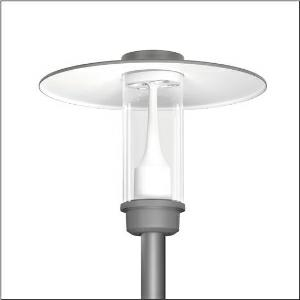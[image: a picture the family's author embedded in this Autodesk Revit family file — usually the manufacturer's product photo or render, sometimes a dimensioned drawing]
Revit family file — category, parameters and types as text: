
# Revit family: litepole_2_iq___p1_0a_5xa5425nf14hp_e36f
name_source: partatom
category: Lighting Fixtures
units: mm (PartAtom-declared; Revit-internal decimal feet)

## family parameters
Cut with Voids When Loaded = No
Host = Face
Light Source = No
Part Type = Normal
Room Calculation Point = No
Round Connector Dimension = Use Diameter
Shared = No

## types (1)
- --- (1 x LED, 4240 lm, 33.6 W, 2700K)
    Apparent Load = 34 VA
    CIE Flux Codes = 32 62 90 96 100
    Color Rendering = 70
    Color Temperature = 2700K
    Default Elevation = 1800 mm
    Description = Litepole 2 iQ, mast luminaire, Module 540 iQ-SR, primary light control with 3 zone facetted reflector, of plastic, silver coated, highly specular, structured, primary optical cover: cover, of PMMA, transparent, light distribution: P1.0a, light emission: direct distribution, primary light characteristic: strongly asymmetric, installation type: post-top, LED, High Power LED, rated luminous flux: 4.240lm, luminous efficacy: 126lm/W, light colour: 727, colour temperature: 2700K, control gear: iQ Street-Remote, control: pre-setting: logarithmic dimming characteristic, Street-Remote, Auto-Match, Temp-Guard, Lumen-Switch, Night-Set, Smart-Wire, Light-Fading, Desk-Remote (wireless, voltage-free reading and setting of iQ features in the workshop via application-optimized NFC function/RFID function), optimised constant luminous flux control (CLO 2.0), with terminal, 6-pole, max. 2.5mm², mains connection: 230..240V, AC, 50/60Hz, start of lifetime: 34W, end of service life: 36W, reduction: 15W, luminaire housing, upper part, of aluminium, coated, Siteco® metallic grey (DB 702S), diameter: 750mm, height: 590mm, spigot size: d x l = 76 x 70mm (post-top) | with reducer (optional accessory) 60 x 70mm, mounting height: 3..5m, post-top mast mounting element, of diecast aluminium, coated, Siteco® metallic grey (DB 702S), Module 540 iQ-SR, traffic white (RAL 9016), equipment: Power, protection rating (complete): IP65, insulation class (complete): insulation class II (safety insulation), certification: CE, ENEC, VDE, packaging unit: 1 piece

Light Distribution: P1.0a
    Height = 590 mm
    Lamp = 1 x LED
    Lamp Light Flux = 4240 lm
    Lamp Power = 33.6 W
    Lamp count = 1
    Length = 750 mm
    Luminous efficacy = 126 lm/W
    Manufacturer = Siteco
    ModVariant = No
    Model = 5XA5425NF14HP
    Number of Poles = 1
    OnlyDefault = Yes
    Power Factor = 1
    Product Name = Litepole 2 iQ | P1.0a
    Product group = mast luminaire | pylon top
    ProductGroupID = 6100
    Protection Class = Protection class II
    Protection Degree = IP 65
    RLX_Detail_Level = 1
    RLX_Emergency_Light_Flux = 0 lm
    RLX_Emergency_Type = 0
    RLX_Emergency_Type_DB = No
    RlxData = <blob elided: 32081 chars, md5=7d2c010b>
    Socket = socket
    Standby Power = 0 W
    System Light Flux = 4240 lm
    System Power = 34 W
    Type Comments = factory setting: luminous flux: 100 % | dim-lin: 254 | 695 mA
    Type Image = l_1006518.jpg
    URL = http://relux.com
    VarID = @adj_151855
    Voltage = 0 V
    Weight = 0.00 kg
    Width = 0 mm  [stored 0 ft]

note: [stored X ft] marks values corroborated as IEEE doubles in the binary element streams (Revit-internal decimal feet)

## geometry (parser evidence)
native form markers: Blend x4, Sweep x9
no freeform markers — native parametric forms only
